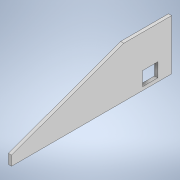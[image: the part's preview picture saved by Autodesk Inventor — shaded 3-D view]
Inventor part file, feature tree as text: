
AUTODESK INVENTOR PART (.ipt)
format: ipt  version: 2021 (Build 250183000, 183)  size: 110,592 bytes
history: native  units: in
note: dims shown in document units (in); Inventor stores cm internally (conversion verified against a paired STEP export)
features: extrude x2, sketch x2
ambient origin geometry x8: Origin, YZ Plane, XZ Plane, XY Plane, X Axis, Y Axis, Z Axis, Center Point
bodies: Solid1 (feature_tree)
feature tree (4):
  extrude  "Extrusion1"  Depth=0.1in TaperAngle=0.0deg
  extrude  "Extrusion2"  Depth=0.433in
  sketch  "Sketch1"  dims[d1=3.75in d2=0.1in d3=0.0in]
  sketch  "Sketch2"  dims[d4=0.1374in d5=0.3in d6=1.5in d7=0.48in d8=0.436in d9=0.1in d10=0.0in d11=0.109in d12=0.433in]
